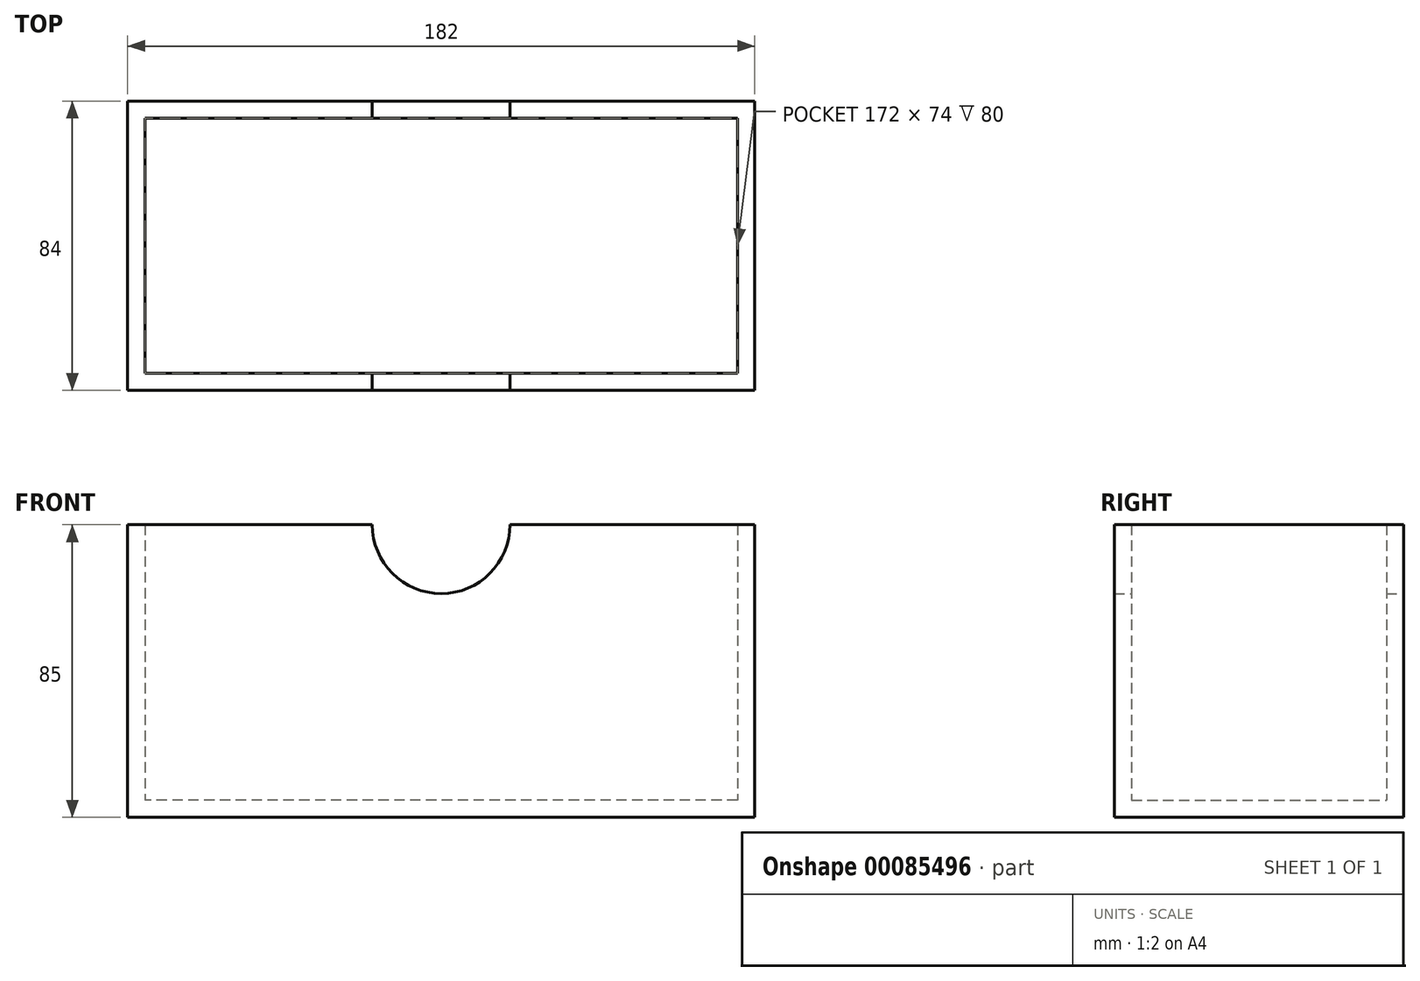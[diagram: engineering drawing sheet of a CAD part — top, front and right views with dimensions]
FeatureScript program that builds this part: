
annotation { "Feature Type Name" : "Feature", "Feature Type Description" : "" }
export const myFeature = defineFeature(function(context is Context, id is Id, definition is map)
    precondition{}
    {
        {
            var Q0;
            Q0=qCreatedBy(makeId("Top.planeOp"),FACE);
            var sketch = newSketch(context, id + "F0", { "sketchPlane" : qUnion([Q0])});
            skLineSegment(sketch, "E0.bottom", {"start": v(0, 0) * mm, "end": v(-182, 0) * mm});
            skLineSegment(sketch, "E0.top", {"start": v(0, -84) * mm, "end": v(-182, -84) * mm});
            skLineSegment(sketch, "E0.left", {"start": v(0, 0) * mm, "end": v(0, -84) * mm});
            skLineSegment(sketch, "E0.right", {"start": v(-182, 0) * mm, "end": v(-182, -84) * mm});
            skPoint(sketch, "E1.endSnap0", {"position": v(-91, 0) * mm});
            skLineSegment(sketch, "E2.bottom", {"start": v(-5, -79) * mm, "end": v(-177, -79) * mm});
            skLineSegment(sketch, "E2.top", {"start": v(-5, -5) * mm, "end": v(-177, -5) * mm});
            skLineSegment(sketch, "E2.left", {"start": v(-5, -79) * mm, "end": v(-5, -5) * mm});
            skLineSegment(sketch, "E2.right", {"start": v(-177, -79) * mm, "end": v(-177, -5) * mm});
            skPoint(sketch, "E1.end.orphan", {"position": v(-91, -5) * mm});
            skPoint(sketch, "E1.start.orphan", {"position": v(-91, 0) * mm});
            skPoint(sketch, "E3.start.orphan", {"position": v(-182, -42) * mm});
            skPoint(sketch, "E4.start.orphan", {"position": v(-91, -84) * mm});
            skSolve(sketch);
        }
        {
            var Q0;
            Q0=makeQuery(id+"F0.imprint","IMPRINT",FACE,{"disambiguationData":[TD([[makeQuery(id+"F0.imprint","IMPRINT",EDGE,{"derivedFrom":sQuery(id+"F0.wireOp",EDGE,"E0.bottom")}),1.0]])]});
            extrude(context, id + "F1", {"entities" : qUnion([Q0]), "depth" : 80 * mm});
        }
        {
            var Q0;
            Q0=qCreatedBy(makeId("Top.planeOp"),FACE);
            var sketch = newSketch(context, id + "F2", { "sketchPlane" : qUnion([Q0])});
            skLineSegment(sketch, "E5.bottom", {"start": v(-182, -84) * mm, "end": v(0, -84) * mm});
            skLineSegment(sketch, "E5.top", {"start": v(-182, 0) * mm, "end": v(0, 0) * mm});
            skLineSegment(sketch, "E5.left", {"start": v(-182, -84) * mm, "end": v(-182, 0) * mm});
            skLineSegment(sketch, "E5.right", {"start": v(0, -84) * mm, "end": v(0, 0) * mm});
            skSolve(sketch);
        }
        {
            var Q0;
            Q0=makeQuery(id+"F2.imprint","IMPRINT",FACE,{"disambiguationData":[TD([[makeQuery(id+"F2.imprint","IMPRINT",EDGE,{"derivedFrom":sQuery(id+"F2.wireOp",EDGE,"E5.bottom")}),1.0]])]});
            extrude(context, id + "F3", {"entities" : qUnion([Q0]), "operationType" : NewBodyOperationType.ADD, "oppositeDirection" : true, "depth" : 5 * mm});
        }
        {
            var Q0;
            Q0=qCreatedBy(makeId("Front.planeOp"),FACE);
            var sketch = newSketch(context, id + "F4", { "sketchPlane" : qUnion([Q0])});
            skLineSegment(sketch, "E6", {"start": v(0, 80) * mm, "end": v(-182, 80) * mm});
            skCircle(sketch, "E7", {"center": v(-91, 80) * mm, "radius": 20 * mm});
            skLineSegment(sketch, "E8", {"start": v(0, 0) * mm, "end": v(0, 80) * mm});
            skSolve(sketch);
        }
        {
            var Q0;
            Q0 = qSketchRegion(id + "F4", true);
            extrude(context, id + "F5", {"entities" : qUnion([Q0]), "operationType" : NewBodyOperationType.REMOVE, "depth" : 90 * mm});
        }
    });
